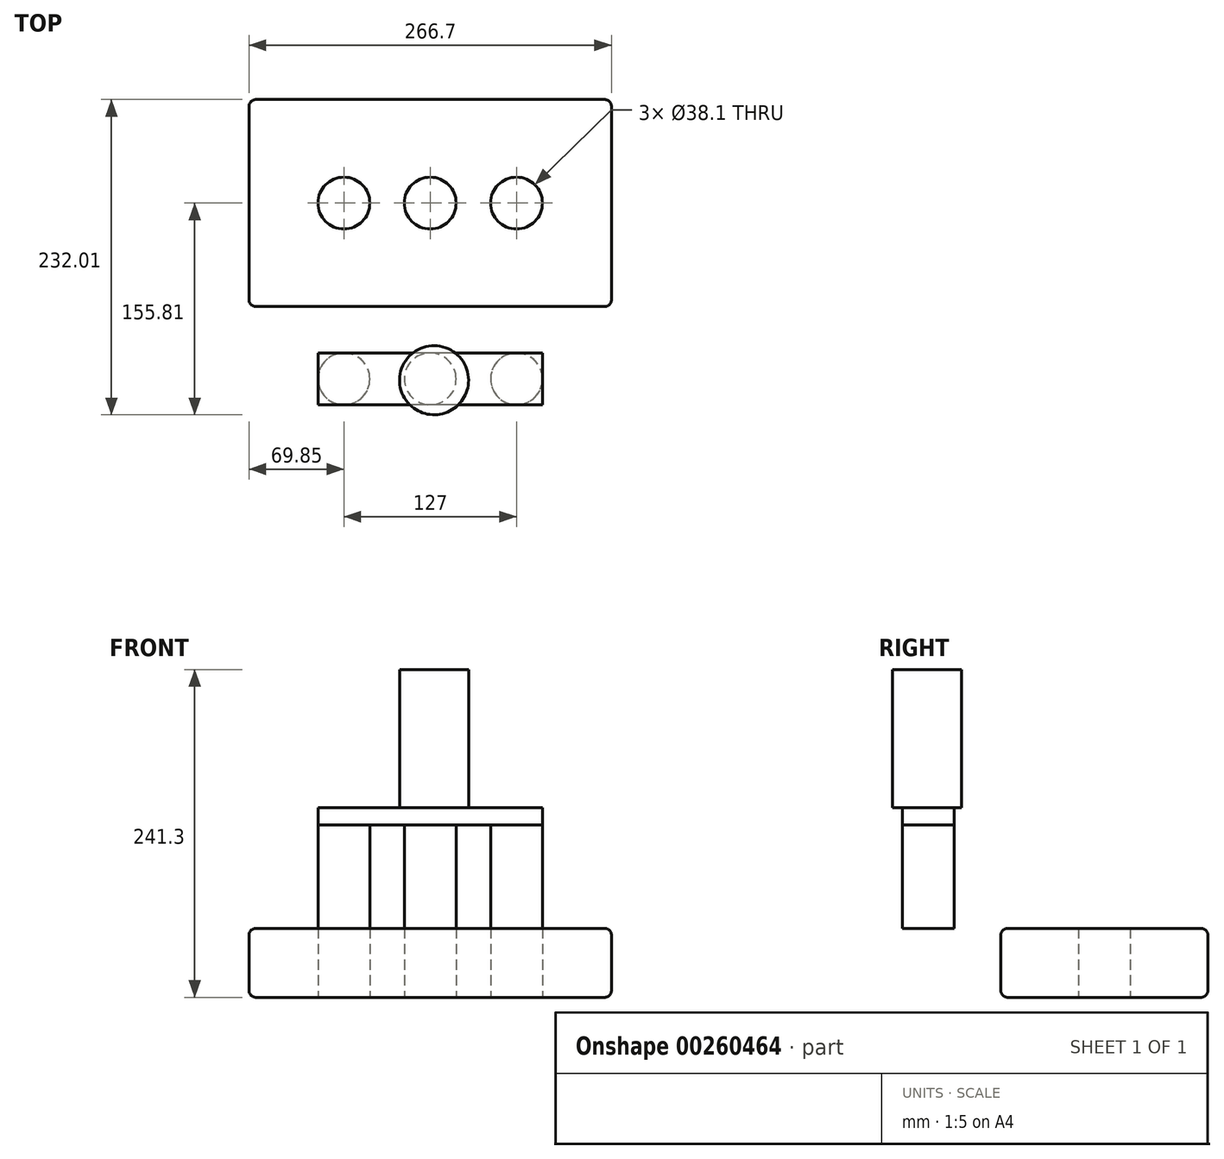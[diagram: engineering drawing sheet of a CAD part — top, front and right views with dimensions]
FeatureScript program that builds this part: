
annotation { "Feature Type Name" : "Feature", "Feature Type Description" : "" }
export const myFeature = defineFeature(function(context is Context, id is Id, definition is map)
    precondition{}
    {
        {
            var Q0;
            Q0=qCreatedBy(makeId("Top.planeOp"),FACE);
            var sketch = newSketch(context, id + "F0", { "sketchPlane" : qUnion([Q0])});
            skLineSegment(sketch, "E0.bottom", {"start": v(133.35, 76.2) * mm, "end": v(-133.35, 76.2) * mm});
            skLineSegment(sketch, "E0.top", {"start": v(133.35, -76.2) * mm, "end": v(-133.35, -76.2) * mm});
            skLineSegment(sketch, "E0.left", {"start": v(133.35, 76.2) * mm, "end": v(133.35, -76.2) * mm});
            skLineSegment(sketch, "E0.right", {"start": v(-133.35, 76.2) * mm, "end": v(-133.35, -76.2) * mm});
            skPoint(sketch, "E0.middle", {"position": v(0, 0) * mm});
            skCircle(sketch, "E1", {"center": v(0, 0) * mm, "radius": 19.05 * mm});
            skCircle(sketch, "E2", {"center": v(63.5, 0) * mm, "radius": 19.05 * mm});
            skCircle(sketch, "E3", {"center": v(-63.5, 0) * mm, "radius": 19.05 * mm});
            skSolve(sketch);
        }
        {
            var Q0;
            Q0=makeQuery(id+"F0.imprint","IMPRINT",FACE,{"disambiguationData":[TD([[makeQuery(id+"F0.imprint","IMPRINT",EDGE,{"derivedFrom":sQuery(id+"F0.wireOp",EDGE,"E0.bottom")}),1.0]])]});
            extrude(context, id + "F1", {"entities" : qUnion([Q0]), "depth" : 50.8 * mm});
        }
        {
            var Q0;
            Q0=makeQuery(id+"F1.opExtrude","SWEPT_FACE",FACE,{"disambiguationData":[OSD([sQuery(id+"F0.wireOp",EDGE,"E0.top")])]});
            var Q1;
            Q1=makeQuery(id+"F1.opExtrude","SWEPT_FACE",FACE,{"disambiguationData":[OSD([sQuery(id+"F0.wireOp",EDGE,"E0.left")])]});
            var Q2;
            Q2=makeQuery(id+"F1.opExtrude","SWEPT_FACE",FACE,{"disambiguationData":[OSD([sQuery(id+"F0.wireOp",EDGE,"E0.bottom")])]});
            var Q3;
            Q3=makeQuery(id+"F1.opExtrude","SWEPT_FACE",FACE,{"disambiguationData":[OSD([sQuery(id+"F0.wireOp",EDGE,"E0.right")])]});
            fillet(context, id + "F2", {"entities" : qUnion([Q0, Q1, Q2, Q3]), "radius" : 5.08 * mm, "tangentPropagation" : true, "allowEdgeOverflow" : false});
        }
        {
            var Q0;
            Q0=makeQuery(id+"F1.opExtrude","CAP_FACE",FACE,{"disambiguationData":[OSD([sQuery(id+"F0.wireOp",EDGE,"E0.bottom"),sQuery(id+"F0.wireOp",EDGE,"E0.top"),sQuery(id+"F0.wireOp",EDGE,"E0.left"),sQuery(id+"F0.wireOp",EDGE,"E0.right"),sQuery(id+"F0.wireOp",EDGE,"E1"),sQuery(id+"F0.wireOp",EDGE,"E2"),sQuery(id+"F0.wireOp",EDGE,"E3")])],"isStart":false});
            var sketch = newSketch(context, id + "F3", { "sketchPlane" : qUnion([Q0])});
            skCircle(sketch, "E4", {"center": v(0, -129.43) * mm, "radius": 19.05 * mm});
            skCircle(sketch, "E5", {"center": v(63.5, -129.43) * mm, "radius": 19.05 * mm});
            skCircle(sketch, "E6", {"center": v(-63.5, -129.43) * mm, "radius": 19.05 * mm});
            skSolve(sketch);
        }
        {
            var Q0;
            Q0=makeQuery(id+"F3.imprint","IMPRINT",FACE,{"disambiguationData":[TD([[makeQuery(id+"F3.imprint","IMPRINT",EDGE,{"derivedFrom":sQuery(id+"F3.wireOp",EDGE,"E6")}),1.0]])]});
            var Q1;
            Q1=makeQuery(id+"F3.imprint","IMPRINT",FACE,{"disambiguationData":[TD([[makeQuery(id+"F3.imprint","IMPRINT",EDGE,{"derivedFrom":sQuery(id+"F3.wireOp",EDGE,"E4")}),1.0]])]});
            var Q2;
            Q2=makeQuery(id+"F3.imprint","IMPRINT",FACE,{"disambiguationData":[TD([[makeQuery(id+"F3.imprint","IMPRINT",EDGE,{"derivedFrom":sQuery(id+"F3.wireOp",EDGE,"E5")}),1.0]])]});
            extrude(context, id + "F4", {"entities" : qUnion([Q0, Q1, Q2]), "depth" : 76.2 * mm});
        }
        {
            var Q0;
            Q0=makeQuery(id+"F4.opExtrude","CAP_FACE",FACE,{"disambiguationData":[OSD([sQuery(id+"F3.wireOp",EDGE,"E6")])],"isStart":false});
            var sketch = newSketch(context, id + "F5", { "sketchPlane" : qUnion([Q0])});
            skLineSegment(sketch, "E7.bottom", {"start": v(82.55, -148.53) * mm, "end": v(-82.55, -148.53) * mm});
            skLineSegment(sketch, "E7.top", {"start": v(82.55, -110.43) * mm, "end": v(-82.55, -110.43) * mm});
            skLineSegment(sketch, "E7.left", {"start": v(82.55, -148.53) * mm, "end": v(82.55, -110.43) * mm});
            skLineSegment(sketch, "E7.right", {"start": v(-82.55, -148.53) * mm, "end": v(-82.55, -110.43) * mm});
            skPoint(sketch, "E7.middle", {"position": v(0, -129.48) * mm});
            skSolve(sketch);
        }
        {
            var Q0;
            {var subQ5=sQuery(id+"F5.wireOp",EDGE,"E7.bottom");Q0=makeQuery(id+"F5.imprint","IMPRINT",FACE,{"disambiguationData":[TD([[makeQuery(id+"F5.imprint","IMPRINT",EDGE,{"derivedFrom":subQ5}),-1.0]])]});}
            var Q1;
            {var subQ0=sQuery(id+"F5.wireOp",EDGE,"E7.right");var subQ1=sQuery(id+"F5.wireOp",EDGE,"E7.top");var subQ2=makeQuery(id+"F5.imprint","INTERSECT",VERTEX,{"derivedFrom":[subQ1,subQ0]});Q1=makeQuery(id+"F5.imprint","IMPRINT",FACE,{"disambiguationData":[TD([[makeQuery(id+"F5.imprint","IMPRINT",EDGE,{"disambiguationData":[TD([[subQ2,1.0]])],"derivedFrom":subQ1}),1.0]])]});}
            var Q2;
            {var subQ0=sQuery(id+"F5.wireOp",EDGE,"E7.top");var subQ1=makeQuery(id+"F4.opExtrude","CAP_EDGE",EDGE,{"disambiguationData":[OSD([sQuery(id+"F3.wireOp",EDGE,"E6")])],"isStart":false});var subQ2=makeQuery(id+"F5.imprint","INTERSECT",VERTEX,{"disambiguationData":[OD(0.0)],"derivedFrom":[subQ1,subQ0]});Q2=makeQuery(id+"F5.imprint","IMPRINT",FACE,{"disambiguationData":[TD([[makeQuery(id+"F5.imprint","IMPRINT",EDGE,{"disambiguationData":[TD([[subQ2,-1.0]])],"derivedFrom":subQ0}),1.0]])]});}
            extrude(context, id + "F6", {"entities" : qUnion([Q0, Q1, Q2]), "depth" : 12.7 * mm});
        }
        {
            var Q0;
            Q0=makeQuery(id+"F6.opExtrude","CAP_FACE",FACE,{"disambiguationData":[OSD([sQuery(id+"F5.wireOp",EDGE,"E7.bottom"),sQuery(id+"F5.wireOp",EDGE,"E7.top"),sQuery(id+"F5.wireOp",EDGE,"E7.left"),sQuery(id+"F5.wireOp",EDGE,"E7.right")])],"isStart":false});
            var sketch = newSketch(context, id + "F7", { "sketchPlane" : qUnion([Q0])});
            skCircle(sketch, "E8", {"center": v(2.8, -130.4) * mm, "radius": 25.4 * mm});
            skSolve(sketch);
        }
        {
            var Q0;
            {var subQ0=sQuery(id+"F7.wireOp",EDGE,"E8");var subQ1=makeQuery(id+"F6.opExtrude","CAP_EDGE",EDGE,{"disambiguationData":[OSD([sQuery(id+"F5.wireOp",EDGE,"E7.top")])],"isStart":false});var subQ2=makeQuery(id+"F7.imprint","INTERSECT",VERTEX,{"disambiguationData":[OD(0.0)],"derivedFrom":[subQ1,subQ0]});Q0=makeQuery(id+"F7.imprint","IMPRINT",FACE,{"disambiguationData":[TD([[makeQuery(id+"F7.imprint","IMPRINT",EDGE,{"disambiguationData":[TD([[subQ2,1.0]])],"derivedFrom":subQ0}),1.0]])]});}
            var Q1;
            {var subQ0=sQuery(id+"F7.wireOp",EDGE,"E8");var subQ1=makeQuery(id+"F6.opExtrude","CAP_EDGE",EDGE,{"disambiguationData":[OSD([sQuery(id+"F5.wireOp",EDGE,"E7.top")])],"isStart":false});var subQ2=makeQuery(id+"F7.imprint","INTERSECT",VERTEX,{"disambiguationData":[OD(0.0)],"derivedFrom":[subQ1,subQ0]});Q1=makeQuery(id+"F7.imprint","IMPRINT",FACE,{"disambiguationData":[TD([[makeQuery(id+"F7.imprint","IMPRINT",EDGE,{"disambiguationData":[TD([[subQ2,-1.0]])],"derivedFrom":subQ0}),1.0]])]});}
            var Q2;
            {var subQ0=sQuery(id+"F7.wireOp",EDGE,"E8");var subQ1=makeQuery(id+"F6.opExtrude","CAP_EDGE",EDGE,{"disambiguationData":[OSD([sQuery(id+"F5.wireOp",EDGE,"E7.bottom")])],"isStart":false});var subQ2=makeQuery(id+"F7.imprint","INTERSECT",VERTEX,{"disambiguationData":[OD(0.0)],"derivedFrom":[subQ1,subQ0]});Q2=makeQuery(id+"F7.imprint","IMPRINT",FACE,{"disambiguationData":[TD([[makeQuery(id+"F7.imprint","IMPRINT",EDGE,{"disambiguationData":[TD([[subQ2,-1.0]])],"derivedFrom":subQ0}),1.0]])]});}
            extrude(context, id + "F8", {"entities" : qUnion([Q0, Q1, Q2]), "operationType" : NewBodyOperationType.ADD, "depth" : 101.6 * mm});
        }
    });
